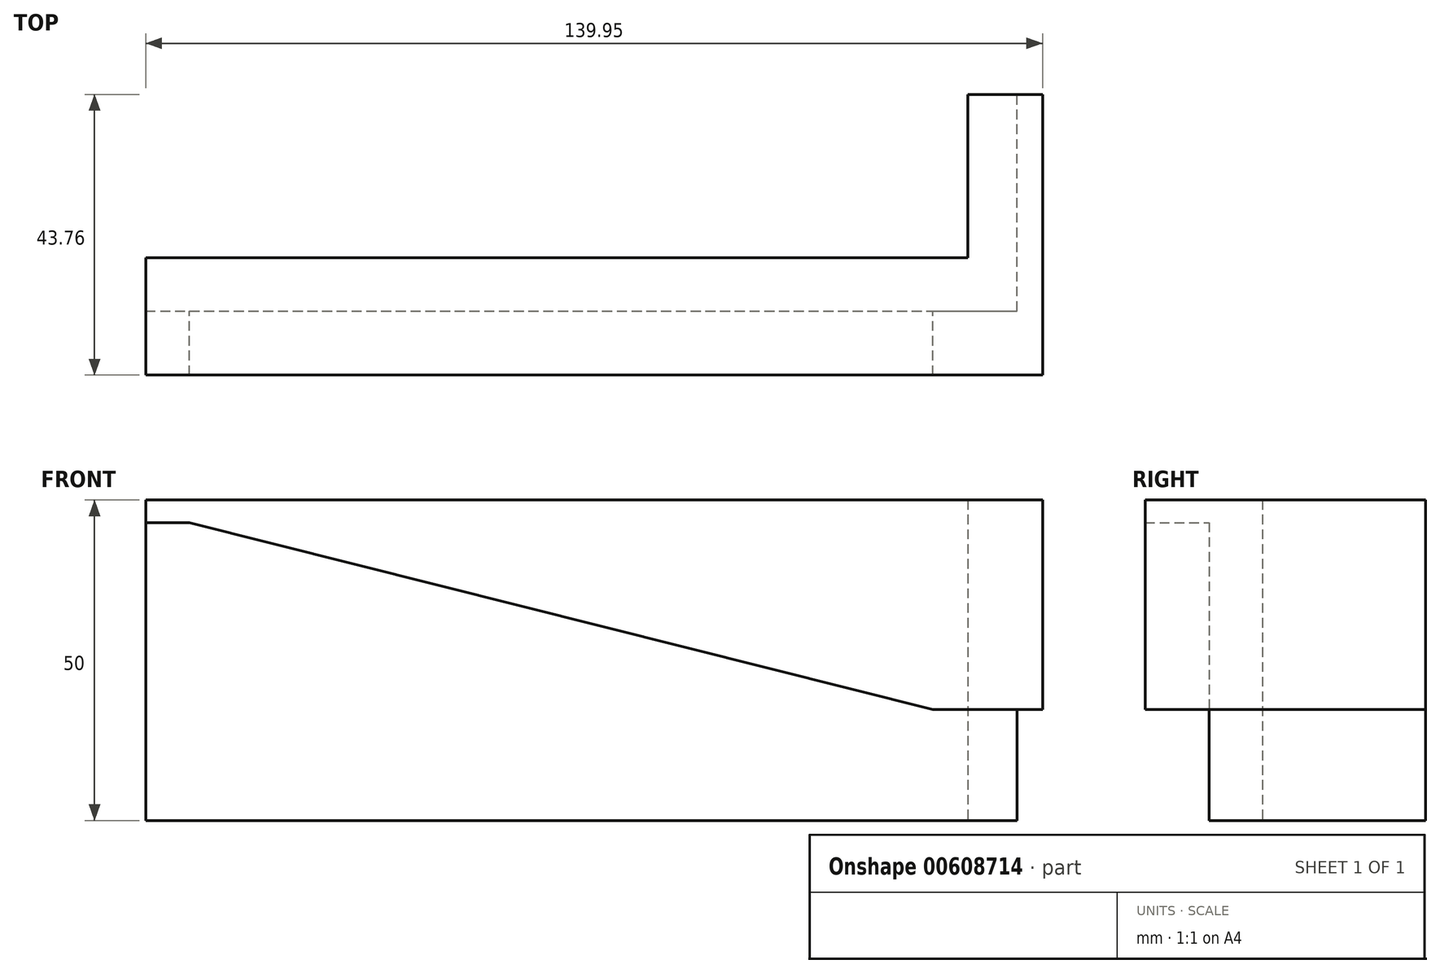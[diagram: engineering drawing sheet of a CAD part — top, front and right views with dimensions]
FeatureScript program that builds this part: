
annotation { "Feature Type Name" : "Feature", "Feature Type Description" : "" }
export const myFeature = defineFeature(function(context is Context, id is Id, definition is map)
    precondition{}
    {
        {
            var Q0;
            Q0=qCreatedBy(makeId("Top.planeOp"),FACE);
            var sketch = newSketch(context, id + "F0", { "sketchPlane" : qUnion([Q0])});
            skLineSegment(sketch, "E0", {"start": v(-65.52, 0) * mm, "end": v(70.43, 0) * mm});
            skLineSegment(sketch, "E1", {"start": v(70.43, 0) * mm, "end": v(70.43, 33.76) * mm});
            skLineSegment(sketch, "E2", {"start": v(70.43, 33.76) * mm, "end": v(62.76, 33.76) * mm});
            skLineSegment(sketch, "E3", {"start": v(62.76, 33.76) * mm, "end": v(62.76, 8.29) * mm});
            skLineSegment(sketch, "E4", {"start": v(62.76, 8.29) * mm, "end": v(-65.52, 8.29) * mm});
            skLineSegment(sketch, "E5", {"start": v(-65.52, 8.29) * mm, "end": v(-65.52, 0) * mm});
            skSolve(sketch);
        }
        {
            var Q0;
            Q0=makeQuery(id+"F0.imprint","IMPRINT",FACE,{"disambiguationData":[TD([[makeQuery(id+"F0.imprint","IMPRINT",EDGE,{"derivedFrom":sQuery(id+"F0.wireOp",EDGE,"E0")}),1.0]])]});
            extrude(context, id + "F1", {"entities" : qUnion([Q0]), "depth" : 50 * mm, "offsetDistance" : 25 * mm});
        }
        {
            var Q0;
            Q0=makeQuery(id+"F1.opExtrude","SWEPT_FACE",FACE,{"disambiguationData":[OSD([sQuery(id+"F0.wireOp",EDGE,"E0")])]});
            var sketch = newSketch(context, id + "F2", { "sketchPlane" : qUnion([Q0])});
            skLineSegment(sketch, "E6", {"start": v(-65.52, 46.48) * mm, "end": v(-58.7, 46.48) * mm});
            skLineSegment(sketch, "E7", {"start": v(-58.7, 46.48) * mm, "end": v(57.31, 17.33) * mm});
            skLineSegment(sketch, "E8", {"start": v(57.31, 17.33) * mm, "end": v(70.43, 17.33) * mm});
            skLineSegment(sketch, "E9", {"start": v(70.43, 17.33) * mm, "end": v(70.43, 50) * mm});
            skLineSegment(sketch, "E10", {"start": v(70.43, 50) * mm, "end": v(-65.52, 50) * mm});
            skLineSegment(sketch, "E11", {"start": v(-65.52, 50) * mm, "end": v(-65.52, 46.48) * mm});
            skSolve(sketch);
        }
        {
            var Q0;
            Q0=makeQuery(id+"F2.imprint","IMPRINT",FACE,{"disambiguationData":[TD([[makeQuery(id+"F2.imprint","IMPRINT",EDGE,{"derivedFrom":sQuery(id+"F2.wireOp",EDGE,"E6")}),1.0]])]});
            extrude(context, id + "F3", {"entities" : qUnion([Q0]), "operationType" : NewBodyOperationType.ADD, "depth" : 10 * mm, "offsetDistance" : 25 * mm});
        }
        {
            var Q0;
            Q0=makeQuery(id+"F3.boolean.opBoolean","MERGE",FACE,{"derivedFrom":[makeQuery(id+"F1.opExtrude","SWEPT_FACE",FACE,{"disambiguationData":[OSD([sQuery(id+"F0.wireOp",EDGE,"E1")])]}),makeQuery(id+"F3.opExtrude","SWEPT_FACE",FACE,{"disambiguationData":[OSD([sQuery(id+"F2.wireOp",EDGE,"E9")])]})]});
            var sketch = newSketch(context, id + "F4", { "sketchPlane" : qUnion([Q0])});
            skLineSegment(sketch, "E12", {"start": v(-10, 50) * mm, "end": v(-10, 17.33) * mm});
            skLineSegment(sketch, "E13", {"start": v(-10, 17.33) * mm, "end": v(33.76, 17.33) * mm});
            skLineSegment(sketch, "E14", {"start": v(33.76, 17.33) * mm, "end": v(33.76, 50) * mm});
            skLineSegment(sketch, "E15", {"start": v(33.76, 50) * mm, "end": v(-10, 50) * mm});
            skSolve(sketch);
        }
        {
            var Q0;
            {var subQ2=sQuery(id+"F4.wireOp",EDGE,"E12");Q0=makeQuery(id+"F4.imprint","IMPRINT",FACE,{"disambiguationData":[TD([[makeQuery(id+"F4.imprint","IMPRINT",EDGE,{"derivedFrom":subQ2}),1.0]])]});}
            extrude(context, id + "F5", {"entities" : qUnion([Q0]), "operationType" : NewBodyOperationType.ADD, "depth" : 4 * mm, "offsetDistance" : 25 * mm});
        }
    });
